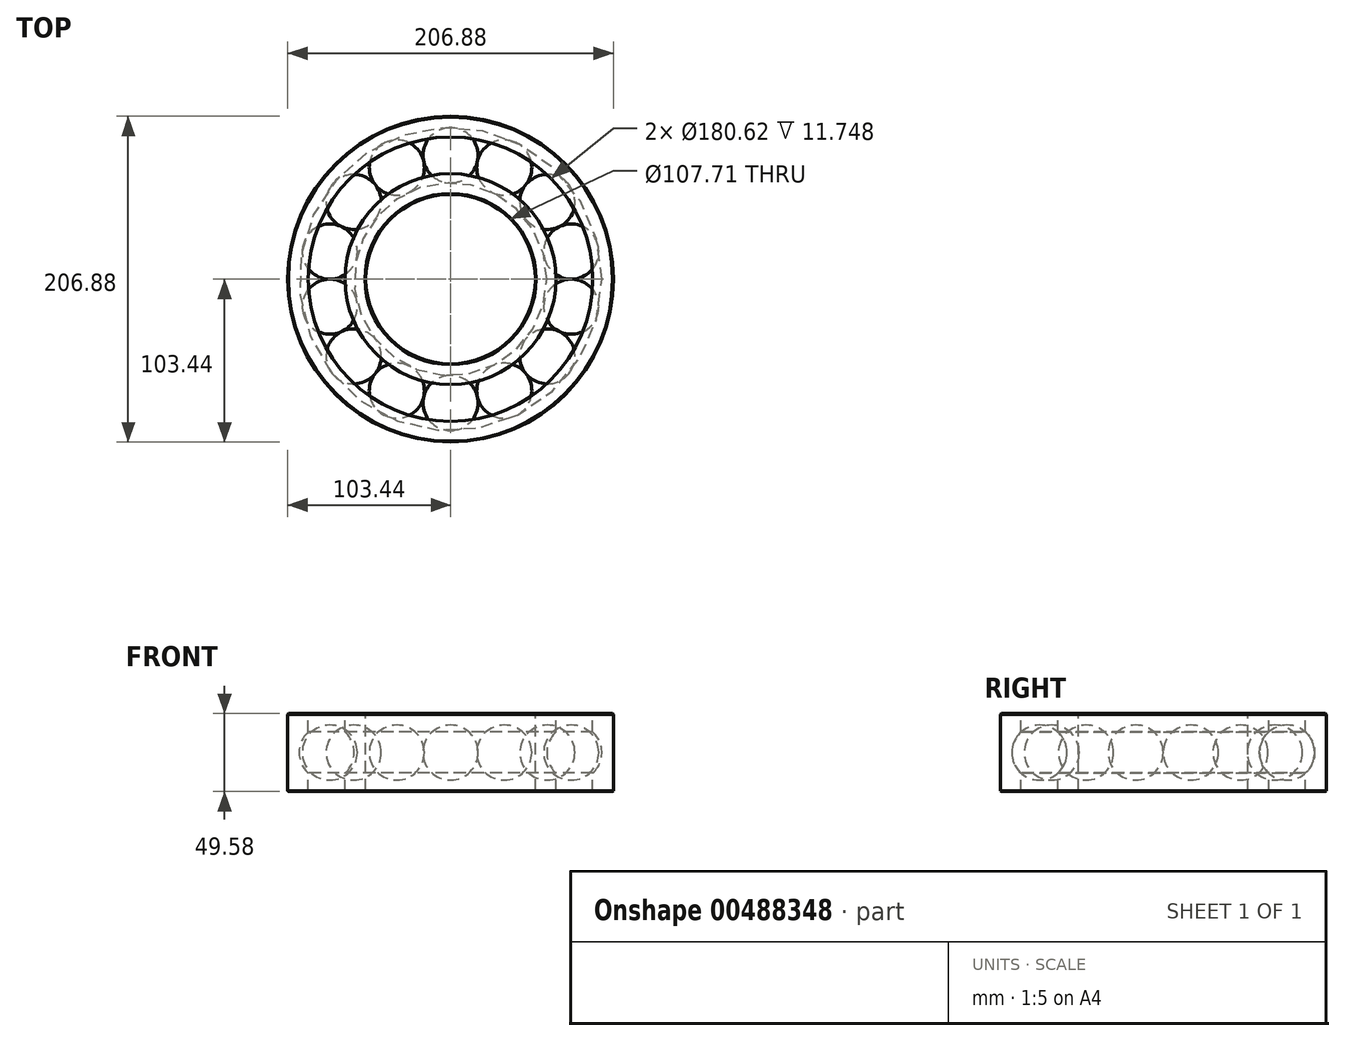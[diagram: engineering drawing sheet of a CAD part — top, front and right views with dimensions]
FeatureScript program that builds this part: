
annotation { "Feature Type Name" : "Feature", "Feature Type Description" : "" }
export const myFeature = defineFeature(function(context is Context, id is Id, definition is map)
    precondition{}
    {
        {
            var Q0;
            Q0=qCreatedBy(makeId("Top.planeOp"),FACE);
            var sketch = newSketch(context, id + "F0", { "sketchPlane" : qUnion([Q0])});
            skCircle(sketch, "E0", {"center": v(0, 0) * mm, "radius": 96.14 * mm});
            skCircle(sketch, "E1", {"center": v(0, 0) * mm, "radius": 61.14 * mm});
            skCircle(sketch, "E2", {"center": v(0, 78.64) * mm, "radius": 17.5 * mm});
            skCircle(sketch, "E3", {"center": v(34.12, 70.86) * mm, "radius": 17.5 * mm});
            skCircle(sketch, "E4", {"center": v(61.49, 49.03) * mm, "radius": 17.5 * mm});
            skCircle(sketch, "E5", {"center": v(76.67, 17.5) * mm, "radius": 17.5 * mm});
            skCircle(sketch, "E6", {"center": v(76.67, -17.5) * mm, "radius": 17.5 * mm});
            skCircle(sketch, "E7", {"center": v(61.49, -49.03) * mm, "radius": 17.5 * mm});
            skCircle(sketch, "E8", {"center": v(34.12, -70.86) * mm, "radius": 17.5 * mm});
            skCircle(sketch, "E9", {"center": v(0, -78.64) * mm, "radius": 17.5 * mm});
            skCircle(sketch, "E10", {"center": v(-34.12, -70.86) * mm, "radius": 17.5 * mm});
            skCircle(sketch, "E11", {"center": v(-61.49, -49.03) * mm, "radius": 17.5 * mm});
            skCircle(sketch, "E12", {"center": v(-76.67, -17.5) * mm, "radius": 17.5 * mm});
            skCircle(sketch, "E13", {"center": v(-76.67, 17.5) * mm, "radius": 17.5 * mm});
            skCircle(sketch, "E14", {"center": v(-61.49, 49.03) * mm, "radius": 17.5 * mm});
            skCircle(sketch, "E15", {"center": v(-34.12, 70.86) * mm, "radius": 17.5 * mm});
            skLineSegment(sketch, "E16", {"start": v(0, 0) * mm, "end": v(0, 96.14) * mm});
            skSolve(sketch);
        }
        {
            var Q0;
            {var subQ1=sQuery(id+"F0.wireOp",EDGE,"E2");var subQ3=makeQuery(id+"F0.imprint","INTERSECT",VERTEX,{"derivedFrom":[subQ1,sQuery(id+"F0.wireOp",EDGE,"E15")]});Q0=makeQuery(id+"F0.imprint","IMPRINT",FACE,{"disambiguationData":[TD([[makeQuery(id+"F0.imprint","IMPRINT",EDGE,{"disambiguationData":[TD([[subQ3,1.0]])],"derivedFrom":subQ1}),1.0]])]});}
            var Q1;
            Q1=sQuery(id+"F0.wireOp",EDGE,"E16");
            revolve(context, id + "F1", {"entities" : qUnion([Q0]), "axis" : qUnion([Q1]), "revolveType" : RevolveType.FULL});
        }
        {
            var Q0;
            Q0=makeQuery(id+"F1.opRevolve","SWEPT_BODY",BODY,{"disambiguationData":[OSD([sQuery(id+"F0.wireOp",EDGE,"E2"),sQuery(id+"F0.wireOp",EDGE,"E16")])]});
            var Q1;
            Q1=sQuery(id+"F0.wireOp",EDGE,"E1");
            circularPattern(context, id + "F2", {"entities" : qUnion([Q0]), "axis" : qUnion([Q1]), "angle" : 360 * degree, "instanceCount" : 14, "equalSpace" : true});
        }
        {
            var Q0;
            Q0=qCreatedBy(makeId("Right.planeOp"),FACE);
            var sketch = newSketch(context, id + "F3", { "sketchPlane" : qUnion([Q0])});
            skLineSegment(sketch, "E17", {"start": v(0, 30) * mm, "end": v(0, -28.56) * mm, "construction": true});
            skCircle(sketch, "E18", {"center": v(78.64, 0) * mm, "radius": 17.5 * mm});
            skLineSegment(sketch, "E19.bottom", {"start": v(103.44, 24.8) * mm, "end": v(-103.44, 24.8) * mm});
            skLineSegment(sketch, "E19.top", {"start": v(103.44, -24.8) * mm, "end": v(-103.44, -24.8) * mm});
            skLineSegment(sketch, "E19.left", {"start": v(103.44, 24.8) * mm, "end": v(103.44, -24.8) * mm});
            skLineSegment(sketch, "E19.right", {"start": v(-103.44, 24.8) * mm, "end": v(-103.44, -24.8) * mm});
            skPoint(sketch, "E19.middle", {"position": v(0, 0) * mm});
            skLineSegment(sketch, "E20", {"start": v(53.85, 24.8) * mm, "end": v(53.85, -24.8) * mm});
            skLineSegment(sketch, "E21", {"start": v(78.64, 24.8) * mm, "end": v(78.64, -24.8) * mm});
            skLineSegment(sketch, "E22.0", {"start": v(90.31, 24.8) * mm, "end": v(90.31, -24.8) * mm});
            skLineSegment(sketch, "E23.0", {"start": v(66.98, 24.8) * mm, "end": v(66.98, -24.8) * mm});
            skLineSegment(sketch, "E24", {"start": v(103.44, 24.8) * mm, "end": v(95.54, -4.55) * mm, "construction": true});
            skLineSegment(sketch, "E25", {"start": v(103.44, 24.8) * mm, "end": v(74.1, 16.9) * mm, "construction": true});
            skLineSegment(sketch, "E26", {"start": v(53.85, -24.8) * mm, "end": v(83.2, -16.9) * mm, "construction": true});
            skLineSegment(sketch, "E27", {"start": v(90.31, 24.8) * mm, "end": v(95.59, 4.38) * mm, "construction": true});
            skSolve(sketch);
        }
        {
            var Q0;
            {var subQ0=sQuery(id+"F3.wireOp",EDGE,"E19.left");Q0=makeQuery(id+"F3.imprint","IMPRINT",FACE,{"disambiguationData":[TD([[makeQuery(id+"F3.imprint","IMPRINT",EDGE,{"derivedFrom":subQ0}),-1.0]])]});}
            var Q1;
            {var subQ0=sQuery(id+"F3.wireOp",EDGE,"E20");Q1=makeQuery(id+"F3.imprint","IMPRINT",FACE,{"disambiguationData":[TD([[makeQuery(id+"F3.imprint","IMPRINT",EDGE,{"derivedFrom":subQ0}),1.0]])]});}
            var Q2;
            Q2=sQuery(id+"F3.wireOp",EDGE,"E17");
            revolve(context, id + "F4", {"entities" : qUnion([Q0, Q1]), "axis" : qUnion([Q2]), "revolveType" : RevolveType.FULL});
        }
        {
            var Q0;
            Q0=makeQuery(id+"F4.opRevolve","SWEPT_EDGE",EDGE,{"disambiguationData":[OSD([sQuery(id+"F3.wireOp",EDGE,"E19.top"),sQuery(id+"F3.wireOp",EDGE,"E19.left")])]});
            var Q1;
            Q1=makeQuery(id+"F4.opRevolve","SWEPT_EDGE",EDGE,{"disambiguationData":[OSD([sQuery(id+"F3.wireOp",EDGE,"E19.bottom"),sQuery(id+"F3.wireOp",EDGE,"E20")])]});
            var Q2;
            Q2=makeQuery(id+"F4.opRevolve","SWEPT_EDGE",EDGE,{"disambiguationData":[OSD([sQuery(id+"F3.wireOp",EDGE,"E19.top"),sQuery(id+"F3.wireOp",EDGE,"E20")])]});
            var Q3;
            Q3=makeQuery(id+"F4.opRevolve","SWEPT_EDGE",EDGE,{"disambiguationData":[OSD([sQuery(id+"F3.wireOp",EDGE,"E19.bottom"),sQuery(id+"F3.wireOp",EDGE,"E19.left")])]});
            chamfer(context, id + "F5", {"entities" : qUnion([Q0, Q1, Q2, Q3]), "width" : .5 * mm, "tangentPropagation" : true});
        }
    });
